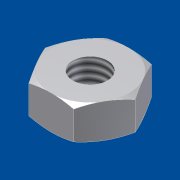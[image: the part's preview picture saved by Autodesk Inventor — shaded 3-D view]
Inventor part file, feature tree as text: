
AUTODESK INVENTOR PART (.ipt)
format: ipt  version: unknown  size: 199,168 bytes
history: native  units: mm
features: sketch x3, projected_geometry x2, extrude x1, hole x1, revolve x1
ambient origin geometry x8: Origin, YZ Plane, XZ Plane, XY Plane, X Axis, Y Axis, Z Axis, Center Point
feature tree (8):
  extrude  "Extrusion1"  Depth=2.4mm TaperAngle=0.0deg
  hole  "Hole1"  [1 undecoded]
  revolve  "Revolution1"  [1 undecoded]
  sketch  "Sketch1"  dims[d0=5.5mm d1=2.4mm d2=0.0mm]
  sketch  "Sketch2"  dims[d3=2.459mm d4=6.0mm d5=4.0mm d6=2.0mm d7=90.0deg d8=8.0mm d9=20.594885mm d10=2.75mm]
  sketch  "Sketch3"  dims[d11=2.75mm d12=4.363323mm d13=4.363323mm d14=90.0deg]
  projected_geometry  "Projected Loop1"
  projected_geometry  "Projected Loop2"
note: 2 required parameter values undecoded (feature->parameter linkage not recoverable at this tier; creation-order binding heuristic only, values carry confidence <= 0.55)